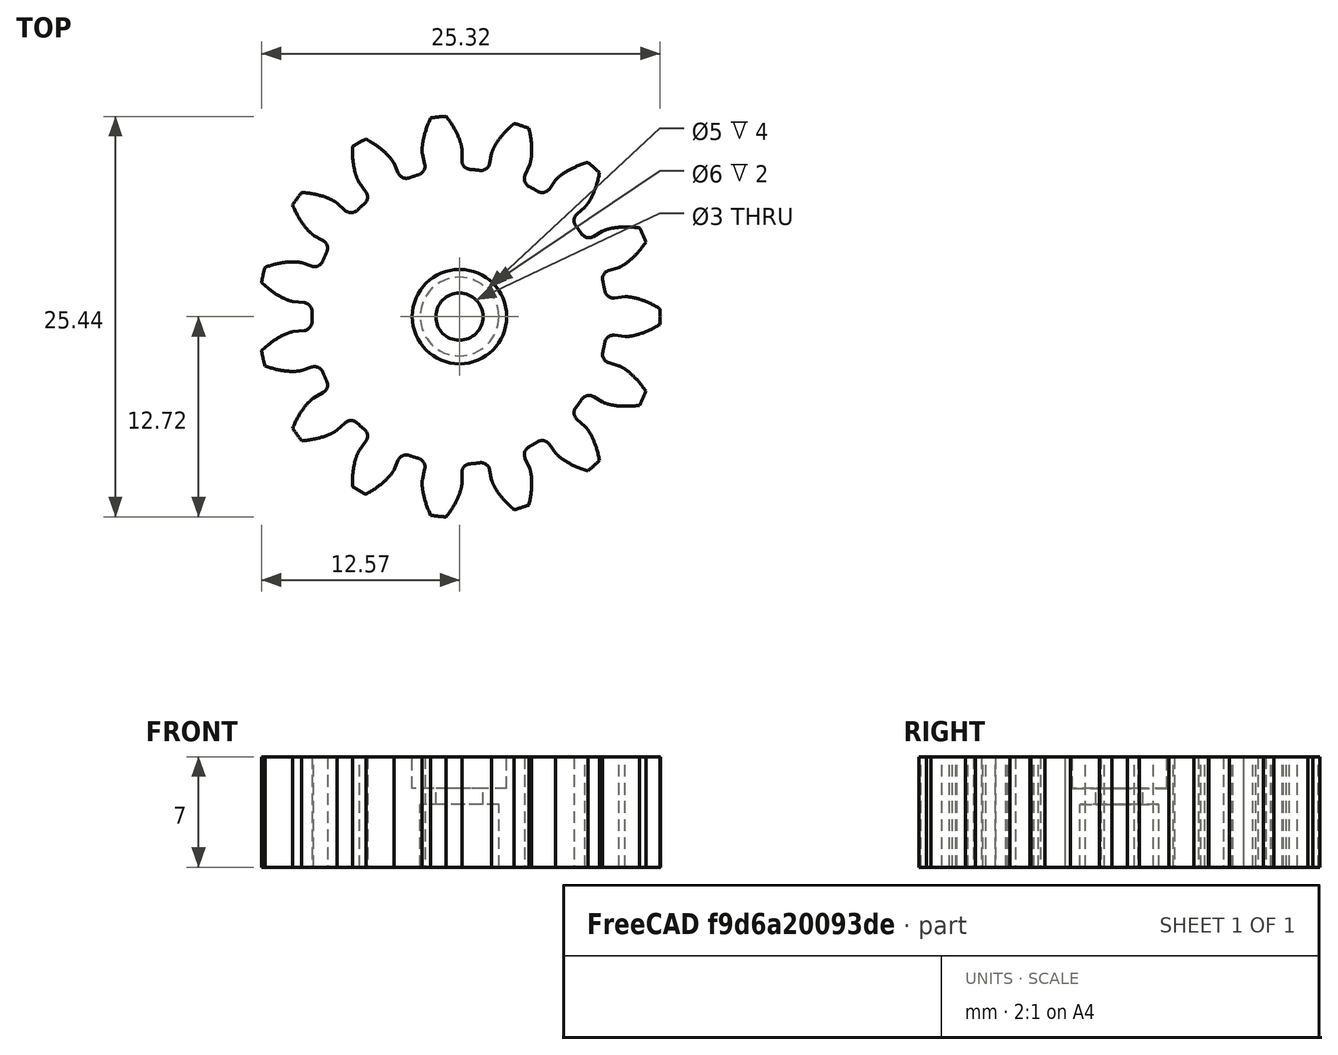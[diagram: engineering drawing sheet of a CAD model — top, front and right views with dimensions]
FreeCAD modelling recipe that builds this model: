
FCSTD DOCUMENT  (FreeCAD 0.19R21123 (Git))
Label: gear
License: Creative Commons Attribution-ShareAlike
LicenseURL: http://creativecommons.org/licenses/by-sa/4.0/
objects: Part::Cylinder×3, Part::MultiFuse×2, Part::Part2DObjectPython×1, Part::Extrusion×1, Part::Cut×1
note: 8 computed .brp shape members not serialized (recipe doc carries the construction recipe); baked Part::Feature solids carry a one-line shape summary decoded from their .brp

FEATURE [Part::Part2DObjectPython] InvoluteGear  # Draft 2D object (typed FeaturePython)
  ExternalGear = true
  HighPrecision = true
  Modules = 1.5
  NumberOfTeeth = 15
  PressureAngle = 20
FEATURE [Part::Extrusion] Extrude  label="solid gear"
  Base = -> InvoluteGear
  Dir = (0,0,1)
  DirMode = 2
  FaceMakerClass = Part::FaceMakerBullseye
  LengthFwd = 7
  LengthRev = 0
  Solid = true
  Symmetric = false
FEATURE [Part::Cylinder] Cylinder
  Angle = 360
  AttacherType = Attacher::AttachEngine3D
  Height = 4
  Radius = 2.5
FEATURE [Part::Cylinder] Cylinder001
  Angle = 360
  AttacherType = Attacher::AttachEngine3D
  Height = 10
  Placement = pos=(0,0,5) rot=(0,0,1;0rad)
  Radius = 3
FEATURE [Part::MultiFuse] Fusion
  Refine = true
  Shapes = -> [Cylinder,Cylinder001]
FEATURE [Part::Cylinder] Cylinder002
  Angle = 360
  AttacherType = Attacher::AttachEngine3D
  Height = 10
  Radius = 1.5
FEATURE [Part::MultiFuse] Fusion001
  Refine = true
  Shapes = -> [Cylinder002,Fusion]
FEATURE [Part::Cut] Cut
  Base = -> Extrude
  Refine = true
  Tool = -> Fusion001
